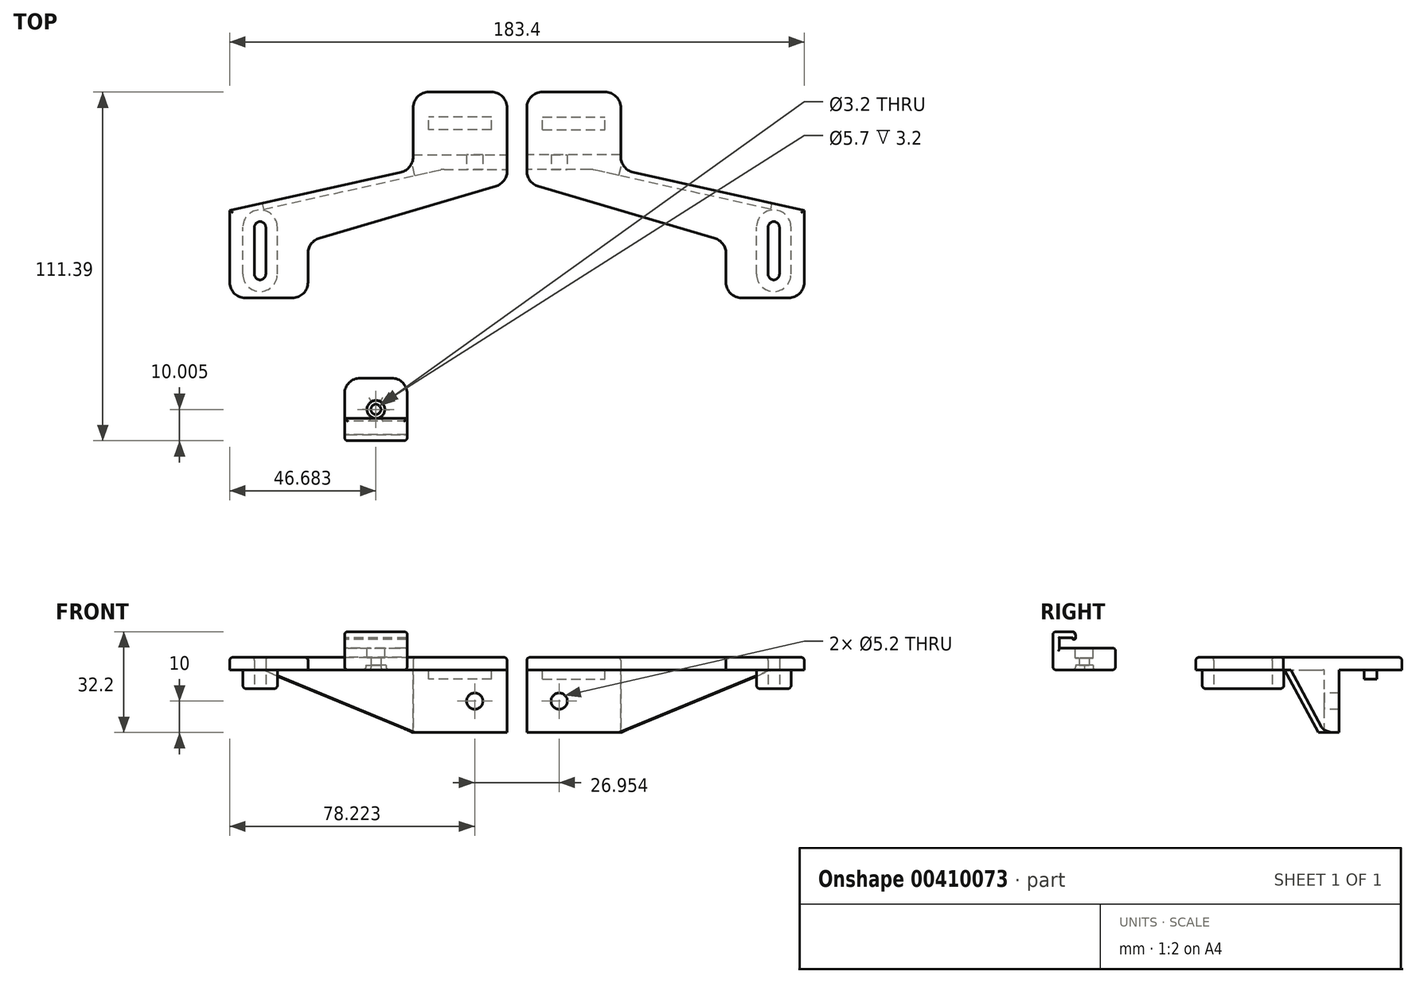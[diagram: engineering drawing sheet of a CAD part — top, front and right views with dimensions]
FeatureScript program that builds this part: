
annotation { "Feature Type Name" : "Feature", "Feature Type Description" : "" }
export const myFeature = defineFeature(function(context is Context, id is Id, definition is map)
    precondition{}
    {
        {
            var Q0;
            Q0=qCreatedBy(makeId("Top.planeOp"),FACE);
            var sketch = newSketch(context, id + "F0", { "sketchPlane" : qUnion([Q0])});
            skLineSegment(sketch, "E0", {"start": v(-33.14, 37.77) * mm, "end": v(-3.14, 37.77) * mm});
            skLineSegment(sketch, "E1", {"start": v(-3.14, 37.77) * mm, "end": v(-3.14, 8.77) * mm});
            skLineSegment(sketch, "E2", {"start": v(-33.14, 13.06) * mm, "end": v(-33.14, 37.77) * mm});
            skCircle(sketch, "E3", {"center": v(-81.98, -20.43) * mm, "radius": 1.8 * mm});
            skCircle(sketch, "E4", {"center": v(-81.98, -5.43) * mm, "radius": 1.8 * mm});
            skLineSegment(sketch, "E5", {"start": v(-83.78, -5.43) * mm, "end": v(-83.78, -20.43) * mm});
            skLineSegment(sketch, "E6", {"start": v(-80.18, -5.43) * mm, "end": v(-80.18, -20.43) * mm});
            skLineSegment(sketch, "E7", {"start": v(-33.14, 13.06) * mm, "end": v(-91.7, 0) * mm});
            skLineSegment(sketch, "E8", {"start": v(-91.7, 0) * mm, "end": v(-91.7, -28) * mm});
            skLineSegment(sketch, "E9", {"start": v(-91.7, -28) * mm, "end": v(-66.7, -28) * mm});
            skLineSegment(sketch, "E10", {"start": v(-66.7, -28) * mm, "end": v(-66.7, -10) * mm});
            skPoint(sketch, "E11.orphan", {"position": v(-33.14, -51.89) * mm});
            skLineSegment(sketch, "E12", {"start": v(-66.7, -10) * mm, "end": v(-3.14, 8.77) * mm});
            skSolve(sketch);
        }
        {
            var Q0;
            Q0=makeQuery(id+"F0.imprint","IMPRINT",FACE,{"disambiguationData":[TD([[makeQuery(id+"F0.imprint","IMPRINT",EDGE,{"derivedFrom":sQuery(id+"F0.wireOp",EDGE,"E0")}),-1.0]])]});
            extrude(context, id + "F1", {"entities" : qUnion([Q0]), "depth" : 4 * mm});
        }
        {
            var Q0;
            Q0=makeQuery(id+"F1.opExtrude","CAP_FACE",FACE,{"disambiguationData":[OSD([sQuery(id+"F0.wireOp",EDGE,"E0"),sQuery(id+"F0.wireOp",EDGE,"E1"),sQuery(id+"F0.wireOp",EDGE,"OpiebKvo-A6Ue-c39r-XeL3-1QtEK74ZUoIi"),sQuery(id+"F0.wireOp",EDGE,"yR2El9kB-Gpyi-T81o-eOrN-Ah2drDqhiUxG"),sQuery(id+"F0.wireOp",EDGE,"FQWpoFjm-FwZp-qIYe-eM8u-l31kpRkj3eQY"),sQuery(id+"F0.wireOp",EDGE,"E2"),sQuery(id+"F0.wireOp",EDGE,"E3"),sQuery(id+"F0.wireOp",EDGE,"E4"),sQuery(id+"F0.wireOp",EDGE,"E5"),sQuery(id+"F0.wireOp",EDGE,"E6")])],"isStart":true});
            var sketch = newSketch(context, id + "F2", { "sketchPlane" : qUnion([Q0])});
            skLineSegment(sketch, "E13", {"start": v(-3.14, -37.77) * mm, "end": v(-33.14, -37.77) * mm});
            skLineSegment(sketch, "E14.bottom", {"start": v(-8.14, -25.77) * mm, "end": v(-28.14, -25.77) * mm});
            skLineSegment(sketch, "E14.top", {"start": v(-8.14, -29.77) * mm, "end": v(-28.14, -29.77) * mm});
            skLineSegment(sketch, "E14.left", {"start": v(-8.14, -25.77) * mm, "end": v(-8.14, -29.77) * mm});
            skLineSegment(sketch, "E14.right", {"start": v(-28.14, -25.77) * mm, "end": v(-28.14, -29.77) * mm});
            skCircle(sketch, "E15", {"center": v(-81.98, 20.43) * mm, "radius": 5.5 * mm});
            skCircle(sketch, "E16", {"center": v(-81.98, 5.43) * mm, "radius": 5.5 * mm});
            skLineSegment(sketch, "E17", {"start": v(-87.48, 20.43) * mm, "end": v(-87.48, 5.43) * mm});
            skLineSegment(sketch, "E18", {"start": v(-76.48, 20.43) * mm, "end": v(-76.48, 5.43) * mm});
            skLineSegment(sketch, "E19", {"start": v(-33.14, -17.77) * mm, "end": v(-3.14, -17.77) * mm});
            skLineSegment(sketch, "E20", {"start": v(-33.14, -13.06) * mm, "end": v(-3.14, -13.06) * mm});
            skLineSegment(sketch, "E21", {"start": v(-81.38, -0.22) * mm, "end": v(-23.81, -13.06) * mm});
            skLineSegment(sketch, "E22", {"start": v(-53.1, -6.53) * mm, "end": v(-49.7, 4.98) * mm});
            skPoint(sketch, "E23", {"position": v(-81.38, -0.22) * mm});
            skLineSegment(sketch, "E24", {"start": v(-81.38, -0.22) * mm, "end": v(-81.82, -2.2) * mm});
            skSolve(sketch);
        }
        {
            var Q0;
            {var subQ0=sQuery(id+"F2.wireOp",EDGE,"E19");Q0=makeQuery(id+"F2.imprint","IMPRINT",FACE,{"disambiguationData":[TD([[makeQuery(id+"F2.imprint","IMPRINT",EDGE,{"derivedFrom":subQ0}),1.0]])]});}
            var Q1;
            Q1=makeQuery(id+"F2.imprint","IMPRINT",FACE,{"disambiguationData":[TD([[makeQuery(id+"F2.imprint","IMPRINT",EDGE,{"derivedFrom":sQuery(id+"F2.wireOp",EDGE,"BE3oNBv8-QwqM-P6IJ-gh2R-psUP1UZXCGw2")}),-1.0]])]});
            var Q2;
            {var subQ1=makeQuery(id+"F1.opExtrude","CAP_EDGE",EDGE,{"disambiguationData":[OSD([sQuery(id+"F0.wireOp",EDGE,"E7")])],"isStart":true});Q2=makeQuery(id+"F2.imprint","IMPRINT",FACE,{"disambiguationData":[TD([[makeQuery(id+"F2.imprint","IMPRINT",EDGE,{"derivedFrom":subQ1}),-1.0]])]});}
            extrude(context, id + "F3", {"entities" : qUnion([Q0, Q1, Q2]), "operationType" : NewBodyOperationType.ADD, "offsetDistance" : 25 * mm, "depth" : 20 * mm});
        }
        {
            var Q0;
            Q0=makeQuery(id+"F2.imprint","IMPRINT",FACE,{"disambiguationData":[TD([[makeQuery(id+"F2.imprint","IMPRINT",EDGE,{"derivedFrom":sQuery(id+"F2.wireOp",EDGE,"E14.bottom")}),1.0]])]});
            extrude(context, id + "F4", {"entities" : qUnion([Q0]), "operationType" : NewBodyOperationType.ADD, "depth" : 3 * mm});
        }
        {
            var Q0;
            Q0=makeQuery(id+"F3.opExtrude","SWEPT_FACE",FACE,{"disambiguationData":[OSD([sQuery(id+"F2.wireOp",EDGE,"E20")])]});
            var sketch = newSketch(context, id + "F5", { "sketchPlane" : qUnion([Q0])});
            skCircle(sketch, "E25", {"center": v(-13.48, -10) * mm, "radius": 2.6 * mm});
            skPoint(sketch, "E25.centerSnap0", {"position": v(-3.14, -10) * mm});
            skPoint(sketch, "E25.centerSnap1", {"position": v(-13.48, 0) * mm});
            skSolve(sketch);
        }
        {
            var Q0;
            Q0=makeQuery(id+"F5.imprint","IMPRINT",FACE,{"disambiguationData":[TD([[makeQuery(id+"F5.imprint","IMPRINT",EDGE,{"derivedFrom":sQuery(id+"F5.wireOp",EDGE,"UfRkS8na-2ZS5-7JHC-9wZ1-n38dNGz8aJN5")}),1.0]])]});
            var Q1;
            Q1=makeQuery(id+"F5.imprint","IMPRINT",FACE,{"disambiguationData":[TD([[makeQuery(id+"F5.imprint","IMPRINT",EDGE,{"derivedFrom":sQuery(id+"F5.wireOp",EDGE,"E25")}),1.0]])]});
            extrude(context, id + "F6", {"entities" : qUnion([Q0, Q1]), "operationType" : NewBodyOperationType.REMOVE, "endBound" : BoundingType.THROUGH_ALL, "oppositeDirection" : true, "depth" : 25 * mm});
        }
        {
            var Q0;
            {var subQ0=makeQuery(id+"F1.opExtrude","CAP_EDGE",EDGE,{"disambiguationData":[OSD([sQuery(id+"F0.wireOp",EDGE,"E3")])],"isStart":true});Q0=makeQuery(id+"F2.imprint","IMPRINT",FACE,{"disambiguationData":[TD([[makeQuery(id+"F2.imprint","IMPRINT",EDGE,{"derivedFrom":subQ0}),1.0]])]});}
            var Q1;
            {var subQ0=sQuery(id+"F2.wireOp",EDGE,"E17");Q1=makeQuery(id+"F2.imprint","IMPRINT",FACE,{"disambiguationData":[TD([[makeQuery(id+"F2.imprint","IMPRINT",EDGE,{"derivedFrom":subQ0}),1.0]])]});}
            var Q2;
            {var subQ0=makeQuery(id+"F1.opExtrude","CAP_EDGE",EDGE,{"disambiguationData":[OSD([sQuery(id+"F0.wireOp",EDGE,"E4")])],"isStart":true});Q2=makeQuery(id+"F2.imprint","IMPRINT",FACE,{"disambiguationData":[TD([[makeQuery(id+"F2.imprint","IMPRINT",EDGE,{"derivedFrom":subQ0}),1.0]])]});}
            var Q3;
            {var subQ0=sQuery(id+"F2.wireOp",EDGE,"E18");Q3=makeQuery(id+"F2.imprint","IMPRINT",FACE,{"disambiguationData":[TD([[makeQuery(id+"F2.imprint","IMPRINT",EDGE,{"derivedFrom":subQ0}),-1.0]])]});}
            extrude(context, id + "F7", {"entities" : qUnion([Q0, Q1, Q2, Q3]), "operationType" : NewBodyOperationType.ADD, "depth" : 6 * mm});
        }
        {
            var Q0;
            Q0=makeQuery(id+"F1.opExtrude","SWEPT_EDGE",EDGE,{"disambiguationData":[OSD([sQuery(id+"F0.wireOp",EDGE,"E0"),sQuery(id+"F0.wireOp",EDGE,"E1")])]});
            var Q1;
            Q1=makeQuery(id+"F1.opExtrude","SWEPT_EDGE",EDGE,{"disambiguationData":[OSD([sQuery(id+"F0.wireOp",EDGE,"E0"),sQuery(id+"F0.wireOp",EDGE,"E2")])]});
            var Q2;
            Q2=makeQuery(id+"F1.opExtrude","SWEPT_EDGE",EDGE,{"disambiguationData":[OSD([sQuery(id+"F0.wireOp",EDGE,"FQWpoFjm-FwZp-qIYe-eM8u-l31kpRkj3eQY"),sQuery(id+"F0.wireOp",EDGE,"E2")])]});
            var Q3;
            Q3=makeQuery(id+"F1.opExtrude","SWEPT_EDGE",EDGE,{"disambiguationData":[OSD([sQuery(id+"F0.wireOp",EDGE,"yR2El9kB-Gpyi-T81o-eOrN-Ah2drDqhiUxG"),sQuery(id+"F0.wireOp",EDGE,"FQWpoFjm-FwZp-qIYe-eM8u-l31kpRkj3eQY")])]});
            var Q4;
            Q4=makeQuery(id+"F1.opExtrude","SWEPT_EDGE",EDGE,{"disambiguationData":[OSD([sQuery(id+"F0.wireOp",EDGE,"OpiebKvo-A6Ue-c39r-XeL3-1QtEK74ZUoIi"),sQuery(id+"F0.wireOp",EDGE,"yR2El9kB-Gpyi-T81o-eOrN-Ah2drDqhiUxG")])]});
            var Q5;
            Q5=makeQuery(id+"F1.opExtrude","SWEPT_EDGE",EDGE,{"disambiguationData":[OSD([sQuery(id+"F0.wireOp",EDGE,"E1"),sQuery(id+"F0.wireOp",EDGE,"OpiebKvo-A6Ue-c39r-XeL3-1QtEK74ZUoIi")])]});
            var Q6;
            Q6=makeQuery(id+"F3.opExtrude","SWEPT_EDGE",EDGE,{"disambiguationData":[OSD([sQuery(id+"F2.wireOp",EDGE,"E20"),sQuery(id+"F2.wireOp",EDGE,"E21")])]});
            var Q7;
            Q7=makeQuery(id+"F1.opExtrude","SWEPT_EDGE",EDGE,{"disambiguationData":[OSD([sQuery(id+"F0.wireOp",EDGE,"E10"),sQuery(id+"F0.wireOp",EDGE,"E12")])]});
            var Q8;
            Q8=makeQuery(id+"F1.opExtrude","SWEPT_EDGE",EDGE,{"disambiguationData":[OSD([sQuery(id+"F0.wireOp",EDGE,"E9"),sQuery(id+"F0.wireOp",EDGE,"E10")])]});
            var Q9;
            Q9=makeQuery(id+"F1.opExtrude","SWEPT_EDGE",EDGE,{"disambiguationData":[OSD([sQuery(id+"F0.wireOp",EDGE,"E8"),sQuery(id+"F0.wireOp",EDGE,"E9")])]});
            fillet(context, id + "F8", {"entities" : qUnion([Q0, Q1, Q2, Q3, Q4, Q5, Q6, Q7, Q8, Q9]), "radius" : 5 * mm, "tangentPropagation" : true, "allowEdgeOverflow" : false});
        }
        {
            var Q0;
            Q0=makeQuery(id+"F1.opExtrude","CAP_FACE",FACE,{"disambiguationData":[OSD([sQuery(id+"F0.wireOp",EDGE,"E0"),sQuery(id+"F0.wireOp",EDGE,"E1"),sQuery(id+"F0.wireOp",EDGE,"OpiebKvo-A6Ue-c39r-XeL3-1QtEK74ZUoIi"),sQuery(id+"F0.wireOp",EDGE,"yR2El9kB-Gpyi-T81o-eOrN-Ah2drDqhiUxG"),sQuery(id+"F0.wireOp",EDGE,"FQWpoFjm-FwZp-qIYe-eM8u-l31kpRkj3eQY"),sQuery(id+"F0.wireOp",EDGE,"E2"),sQuery(id+"F0.wireOp",EDGE,"E3"),sQuery(id+"F0.wireOp",EDGE,"E4"),sQuery(id+"F0.wireOp",EDGE,"E5"),sQuery(id+"F0.wireOp",EDGE,"E6")])],"isStart":false});
            var Q1;
            Q1=makeQuery(id+"F3.opExtrude","CAP_EDGE",EDGE,{"disambiguationData":[OSD([sQuery(id+"F2.wireOp",EDGE,"E13")])],"isStart":true});
            var Q2;
            Q2=makeQuery(id+"F7.opExtrude","CAP_EDGE",EDGE,{"disambiguationData":[OSD([sQuery(id+"F2.wireOp",EDGE,"E17")])],"isStart":true});
            var Q3;
            Q3=makeQuery(id+"F7.opExtrude","CAP_EDGE",EDGE,{"disambiguationData":[OSD([sQuery(id+"F2.wireOp",EDGE,"E17")])],"isStart":false});
            fillet(context, id + "F9", {"entities" : qUnion([Q0, Q1, Q2, Q3]), "radius" : 1 * mm, "tangentPropagation" : true, "allowEdgeOverflow" : false});
        }
        {
            var Q0;
            Q0=makeQuery(id+"F3.opExtrude","CAP_EDGE",EDGE,{"disambiguationData":[OSD([sQuery(id+"F2.wireOp",EDGE,"E24")])],"isStart":false});
            chamfer(context, id + "F10", {"entities" : qUnion([Q0]), "chamferType" : ChamferType.OFFSET_ANGLE, "width" : 50 * mm, "oppositeDirection" : false, "angle" : 22 * degree, "tangentPropagation" : true});
        }
        {
            var Q0;
            Q0=makeQuery(id+"F1.opExtrude","SWEPT_BODY",BODY,{"disambiguationData":[OSD([sQuery(id+"F0.wireOp",EDGE,"E0"),sQuery(id+"F0.wireOp",EDGE,"E1"),sQuery(id+"F0.wireOp",EDGE,"OpiebKvo-A6Ue-c39r-XeL3-1QtEK74ZUoIi"),sQuery(id+"F0.wireOp",EDGE,"yR2El9kB-Gpyi-T81o-eOrN-Ah2drDqhiUxG"),sQuery(id+"F0.wireOp",EDGE,"FQWpoFjm-FwZp-qIYe-eM8u-l31kpRkj3eQY"),sQuery(id+"F0.wireOp",EDGE,"E2"),sQuery(id+"F0.wireOp",EDGE,"E3"),sQuery(id+"F0.wireOp",EDGE,"E4"),sQuery(id+"F0.wireOp",EDGE,"E5"),sQuery(id+"F0.wireOp",EDGE,"E6")])]});
            var Q1;
            Q1=qCreatedBy(makeId("Right.planeOp"),FACE);
            mirror(context, id + "F11", {"entities" : qUnion([Q0]), "mirrorPlane" : qUnion([Q1])});
        }
        {
            var Q0;
            Q0=qCreatedBy(makeId("Top.planeOp"),FACE);
            var sketch = newSketch(context, id + "F12", { "sketchPlane" : qUnion([Q0])});
            skLineSegment(sketch, "E26.bottom", {"start": v(-55.02, -53.62) * mm, "end": v(-35.02, -53.62) * mm});
            skLineSegment(sketch, "E26.top", {"start": v(-55.02, -73.62) * mm, "end": v(-35.02, -73.62) * mm});
            skLineSegment(sketch, "E26.left", {"start": v(-55.02, -53.62) * mm, "end": v(-55.02, -73.62) * mm});
            skLineSegment(sketch, "E26.right", {"start": v(-35.02, -53.62) * mm, "end": v(-35.02, -73.62) * mm});
            skCircle(sketch, "E27", {"center": v(-45.02, -63.62) * mm, "radius": 1.6 * mm});
            skPoint(sketch, "E27.centerSnap0", {"position": v(-55.02, -63.62) * mm});
            skPoint(sketch, "E27.centerSnap1", {"position": v(-45.02, -53.62) * mm});
            skSolve(sketch);
        }
        {
            var Q0;
            Q0=qSketchRegion(id+"F12",true);
            extrude(context, id + "F13", {"entities" : qUnion([Q0]), "depth" : 7 * mm});
        }
        {
            var Q0;
            Q0=makeQuery(id+"F13.opExtrude","CAP_FACE",FACE,{"disambiguationData":[OSD([sQuery(id+"F12.wireOp",EDGE,"E26.bottom"),sQuery(id+"F12.wireOp",EDGE,"E26.top"),sQuery(id+"F12.wireOp",EDGE,"E26.left"),sQuery(id+"F12.wireOp",EDGE,"E26.right"),sQuery(id+"F12.wireOp",EDGE,"E27")])],"isStart":false});
            var sketch = newSketch(context, id + "F14", { "sketchPlane" : qUnion([Q0])});
            skCircle(sketch, "E28", {"center": v(-45.02, -63.62) * mm, "radius": 2.85 * mm});
            skLineSegment(sketch, "E29", {"start": v(-55.02, -71.62) * mm, "end": v(-35.02, -71.62) * mm});
            skSolve(sketch);
        }
        {
            var Q0;
            Q0=makeQuery(id+"F14.imprint","IMPRINT",FACE,{"disambiguationData":[TD([[makeQuery(id+"F14.imprint","IMPRINT",EDGE,{"derivedFrom":sQuery(id+"F14.wireOp",EDGE,"E28")}),1.0]])]});
            extrude(context, id + "F15", {"entities" : qUnion([Q0]), "operationType" : NewBodyOperationType.REMOVE, "oppositeDirection" : true, "depth" : 3.2 * mm});
        }
        {
            var Q0;
            Q0=makeQuery(id+"F13.opExtrude","CAP_FACE",FACE,{"disambiguationData":[OSD([sQuery(id+"F12.wireOp",EDGE,"E26.bottom"),sQuery(id+"F12.wireOp",EDGE,"E26.top"),sQuery(id+"F12.wireOp",EDGE,"E26.left"),sQuery(id+"F12.wireOp",EDGE,"E26.right"),sQuery(id+"F12.wireOp",EDGE,"E27")])],"isStart":true});
            var sketch = newSketch(context, id + "F16", { "sketchPlane" : qUnion([Q0])});
            skCircle(sketch, "E30.cCircle", {"center": v(-45.02, 63.62) * mm, "radius": 2.8 * mm, "construction": true});
            skLineSegment(sketch, "E30.0", {"start": v(-46.63, 66.42) * mm, "end": v(-43.4, 66.42) * mm});
            skLineSegment(sketch, "E30.1", {"start": v(-43.4, 66.42) * mm, "end": v(-41.78, 63.62) * mm});
            skLineSegment(sketch, "E30.2", {"start": v(-41.78, 63.62) * mm, "end": v(-43.4, 60.82) * mm});
            skLineSegment(sketch, "E30.3", {"start": v(-43.4, 60.82) * mm, "end": v(-46.63, 60.82) * mm});
            skLineSegment(sketch, "E30.4", {"start": v(-46.63, 60.82) * mm, "end": v(-48.25, 63.62) * mm});
            skLineSegment(sketch, "E30.5", {"start": v(-48.25, 63.62) * mm, "end": v(-46.63, 66.42) * mm});
            skPoint(sketch, "E30.0.midPoint", {"position": v(-45.02, 66.42) * mm});
            skSolve(sketch);
        }
        {
            var Q0;
            Q0=makeQuery(id+"F16.imprint","IMPRINT",FACE,{"disambiguationData":[TD([[makeQuery(id+"F16.imprint","IMPRINT",EDGE,{"derivedFrom":sQuery(id+"F16.wireOp",EDGE,"E30.0")}),-1.0]])]});
            extrude(context, id + "F17", {"entities" : qUnion([Q0]), "operationType" : NewBodyOperationType.REMOVE, "oppositeDirection" : true, "depth" : 1.5 * mm});
        }
        {
            var Q0;
            {var subQ0=sQuery(id+"F14.wireOp",EDGE,"E29");Q0=makeQuery(id+"F14.imprint","IMPRINT",FACE,{"disambiguationData":[TD([[makeQuery(id+"F14.imprint","IMPRINT",EDGE,{"derivedFrom":subQ0}),-1.0]])]});}
            extrude(context, id + "F18", {"entities" : qUnion([Q0]), "operationType" : NewBodyOperationType.ADD, "depth" : 5.2 * mm});
        }
        {
            var Q0;
            Q0=makeQuery(id+"F18.opExtrude","SWEPT_FACE",FACE,{"disambiguationData":[OSD([sQuery(id+"F14.wireOp",EDGE,"E29")])]});
            var sketch = newSketch(context, id + "F19", { "sketchPlane" : qUnion([Q0])});
            skLineSegment(sketch, "E31", {"start": v(35.02, 10.2) * mm, "end": v(55.02, 10.2) * mm});
            skSolve(sketch);
        }
        {
            var Q0;
            {var subQ0=sQuery(id+"F19.wireOp",EDGE,"E31");Q0=makeQuery(id+"F19.imprint","IMPRINT",FACE,{"disambiguationData":[TD([[makeQuery(id+"F19.imprint","IMPRINT",EDGE,{"derivedFrom":subQ0}),1.0]])]});}
            extrude(context, id + "F20", {"entities" : qUnion([Q0]), "operationType" : NewBodyOperationType.ADD, "depth" : 5.2 * mm});
        }
        {
            var Q0;
            Q0=makeQuery(id+"F20.opExtrude","SWEPT_FACE",FACE,{"disambiguationData":[OSD([sQuery(id+"F19.wireOp",EDGE,"E31")])]});
            var sketch = newSketch(context, id + "F21", { "sketchPlane" : qUnion([Q0])});
            skLineSegment(sketch, "E32", {"start": v(-35.02, 67.42) * mm, "end": v(-55.02, 67.42) * mm});
            skPoint(sketch, "E32.endSnap0", {"position": v(-55.02, 69.02) * mm});
            skSolve(sketch);
        }
        {
            var Q0;
            {var subQ0=sQuery(id+"F21.wireOp",EDGE,"E32");Q0=makeQuery(id+"F21.imprint","IMPRINT",FACE,{"disambiguationData":[TD([[makeQuery(id+"F21.imprint","IMPRINT",EDGE,{"derivedFrom":subQ0}),1.0]])]});}
            extrude(context, id + "F22", {"entities" : qUnion([Q0]), "operationType" : NewBodyOperationType.ADD, "depth" : 0.4 * mm});
        }
        {
            var Q0;
            Q0=makeQuery(id+"F13.opExtrude","SWEPT_EDGE",EDGE,{"disambiguationData":[OSD([sQuery(id+"F12.wireOp",EDGE,"E26.bottom"),sQuery(id+"F12.wireOp",EDGE,"E26.right")])]});
            var Q1;
            Q1=makeQuery(id+"F13.opExtrude","SWEPT_EDGE",EDGE,{"disambiguationData":[OSD([sQuery(id+"F12.wireOp",EDGE,"E26.bottom"),sQuery(id+"F12.wireOp",EDGE,"E26.left")])]});
            fillet(context, id + "F23", {"entities" : qUnion([Q0, Q1]), "radius" : 5 * mm, "tangentPropagation" : true, "allowEdgeOverflow" : false});
        }
        {
            var Q0;
            Q0=makeQuery(id+"F15.boolean.opBoolean","COPY",EDGE,{"derivedFrom":makeQuery(id+"F15.opExtrude","CAP_EDGE",EDGE,{"disambiguationData":[OSD([sQuery(id+"F14.wireOp",EDGE,"E28")])],"isStart":true})});
            var Q1;
            Q1=makeQuery(id+"F18.opExtrude","CAP_EDGE",EDGE,{"disambiguationData":[OSD([sQuery(id+"F12.wireOp",EDGE,"E26.top")])],"isStart":false});
            var Q2;
            Q2=makeQuery(id+"F20.opExtrude","CAP_EDGE",EDGE,{"disambiguationData":[OSD([sQuery(id+"F14.wireOp",EDGE,"E29")])],"isStart":false});
            var Q3;
            Q3=makeQuery(id+"F13.opExtrude","CAP_EDGE",EDGE,{"disambiguationData":[OSD([sQuery(id+"F12.wireOp",EDGE,"E26.right")])],"isStart":false});
            var Q4;
            Q4=makeQuery(id+"F13.opExtrude","CAP_EDGE",EDGE,{"disambiguationData":[OSD([sQuery(id+"F12.wireOp",EDGE,"E26.bottom")])],"isStart":false});
            var Q5;
            {var subQ0=sQuery(id+"F12.wireOp",EDGE,"E26.right");var subQ1=sQuery(id+"F12.wireOp",EDGE,"E26.bottom");Q5=makeQuery(id+"F23.opFillet","BLEND_EDGE",EDGE,{"blendedFrom":[makeQuery(id+"F13.opExtrude","SWEPT_EDGE",EDGE,{"disambiguationData":[OSD([subQ1,subQ0])]}),makeQuery(id+"F13.opExtrude","CAP_FACE",FACE,{"disambiguationData":[OSD([subQ1,sQuery(id+"F12.wireOp",EDGE,"E26.top"),sQuery(id+"F12.wireOp",EDGE,"E26.left"),subQ0,sQuery(id+"F12.wireOp",EDGE,"E27")])],"isStart":false})],"blendedInto":[makeQuery(id+"F13.opExtrude","CAP_FACE",FACE,{"disambiguationData":[OSD([subQ1,sQuery(id+"F12.wireOp",EDGE,"E26.top"),sQuery(id+"F12.wireOp",EDGE,"E26.left"),subQ0,sQuery(id+"F12.wireOp",EDGE,"E27")])],"isStart":false})]});}
            var Q6;
            Q6=makeQuery(id+"F13.opExtrude","CAP_EDGE",EDGE,{"disambiguationData":[OSD([sQuery(id+"F12.wireOp",EDGE,"E26.left")])],"isStart":false});
            var Q7;
            {var subQ0=sQuery(id+"F12.wireOp",EDGE,"E26.left");var subQ1=sQuery(id+"F12.wireOp",EDGE,"E26.bottom");Q7=makeQuery(id+"F23.opFillet","BLEND_EDGE",EDGE,{"blendedFrom":[makeQuery(id+"F13.opExtrude","SWEPT_EDGE",EDGE,{"disambiguationData":[OSD([subQ1,subQ0])]}),makeQuery(id+"F13.opExtrude","CAP_FACE",FACE,{"disambiguationData":[OSD([subQ1,sQuery(id+"F12.wireOp",EDGE,"E26.top"),subQ0,sQuery(id+"F12.wireOp",EDGE,"E26.right"),sQuery(id+"F12.wireOp",EDGE,"E27")])],"isStart":false})],"blendedInto":[makeQuery(id+"F13.opExtrude","CAP_FACE",FACE,{"disambiguationData":[OSD([subQ1,sQuery(id+"F12.wireOp",EDGE,"E26.top"),subQ0,sQuery(id+"F12.wireOp",EDGE,"E26.right"),sQuery(id+"F12.wireOp",EDGE,"E27")])],"isStart":false})]});}
            var Q8;
            Q8=makeQuery(id+"F13.opExtrude","CAP_FACE",FACE,{"disambiguationData":[OSD([sQuery(id+"F12.wireOp",EDGE,"E26.bottom"),sQuery(id+"F12.wireOp",EDGE,"E26.top"),sQuery(id+"F12.wireOp",EDGE,"E26.left"),sQuery(id+"F12.wireOp",EDGE,"E26.right"),sQuery(id+"F12.wireOp",EDGE,"E27")])],"isStart":true});
            var Q9;
            {var subQ0=sQuery(id+"F12.wireOp",EDGE,"E26.right");var subQ1=sQuery(id+"F12.wireOp",EDGE,"E26.top");Q9=makeQuery(id+"F18.boolean.opBoolean","MERGE",EDGE,{"derivedFrom":[makeQuery(id+"F13.opExtrude","SWEPT_EDGE",EDGE,{"disambiguationData":[OSD([subQ1,subQ0])]}),makeQuery(id+"F18.opExtrude","SWEPT_EDGE",EDGE,{"disambiguationData":[OSD([subQ1,subQ0])]})]});}
            var Q10;
            {var subQ0=sQuery(id+"F12.wireOp",EDGE,"E26.left");var subQ1=sQuery(id+"F12.wireOp",EDGE,"E26.top");Q10=makeQuery(id+"F18.boolean.opBoolean","MERGE",EDGE,{"derivedFrom":[makeQuery(id+"F13.opExtrude","SWEPT_EDGE",EDGE,{"disambiguationData":[OSD([subQ1,subQ0])]}),makeQuery(id+"F18.opExtrude","SWEPT_EDGE",EDGE,{"disambiguationData":[OSD([subQ1,subQ0])]})]});}
            var Q11;
            {var subQ0=sQuery(id+"F12.wireOp",EDGE,"E26.left");Q11=makeQuery(id+"F20.boolean.opBoolean","MERGE",EDGE,{"derivedFrom":[makeQuery(id+"F18.opExtrude","CAP_EDGE",EDGE,{"disambiguationData":[OSD([subQ0])],"isStart":false}),makeQuery(id+"F20.opExtrude","SWEPT_EDGE",EDGE,{"disambiguationData":[OSD([subQ0,sQuery(id+"F14.wireOp",EDGE,"E29")])]})]});}
            var Q12;
            {var subQ0=sQuery(id+"F12.wireOp",EDGE,"E26.right");Q12=makeQuery(id+"F20.boolean.opBoolean","MERGE",EDGE,{"derivedFrom":[makeQuery(id+"F18.opExtrude","CAP_EDGE",EDGE,{"disambiguationData":[OSD([subQ0])],"isStart":false}),makeQuery(id+"F20.opExtrude","SWEPT_EDGE",EDGE,{"disambiguationData":[OSD([subQ0,sQuery(id+"F14.wireOp",EDGE,"E29")])]})]});}
            fillet(context, id + "F24", {"entities" : qUnion([Q0, Q1, Q2, Q3, Q4, Q5, Q6, Q7, Q8, Q9, Q10, Q11, Q12]), "radius" : 1 * mm, "allowEdgeOverflow" : false});
        }
        {
            var Q0;
            Q0=makeQuery(id+"F18.opExtrude","SWEPT_EDGE",EDGE,{"disambiguationData":[OSD([sQuery(id+"F12.wireOp",EDGE,"E26.right"),sQuery(id+"F14.wireOp",EDGE,"E29")])]});
            var Q1;
            Q1=makeQuery(id+"F20.opExtrude","SWEPT_EDGE",EDGE,{"disambiguationData":[OSD([sQuery(id+"F12.wireOp",EDGE,"E26.right"),sQuery(id+"F14.wireOp",EDGE,"E29"),sQuery(id+"F19.wireOp",EDGE,"E31")])]});
            var Q2;
            Q2=makeQuery(id+"F22.opExtrude","CAP_EDGE",EDGE,{"disambiguationData":[OSD([sQuery(id+"F12.wireOp",EDGE,"E26.right"),sQuery(id+"F14.wireOp",EDGE,"E29"),sQuery(id+"F19.wireOp",EDGE,"E31")])],"isStart":false});
            var Q3;
            Q3=makeQuery(id+"F22.opExtrude","SWEPT_EDGE",EDGE,{"disambiguationData":[OSD([sQuery(id+"F12.wireOp",EDGE,"E26.right"),sQuery(id+"F14.wireOp",EDGE,"E29"),sQuery(id+"F19.wireOp",EDGE,"E31"),sQuery(id+"F21.wireOp",EDGE,"E32")])]});
            var Q4;
            {var subQ0=sQuery(id+"F14.wireOp",EDGE,"E29");var subQ1=sQuery(id+"F12.wireOp",EDGE,"E26.right");Q4=makeQuery(id+"F22.boolean.opBoolean","MERGE",EDGE,{"derivedFrom":[makeQuery(id+"F20.opExtrude","CAP_EDGE",EDGE,{"disambiguationData":[OSD([subQ1,subQ0])],"isStart":false}),makeQuery(id+"F22.opExtrude","SWEPT_EDGE",EDGE,{"disambiguationData":[OSD([subQ1,subQ0,sQuery(id+"F19.wireOp",EDGE,"E31")])]})]});}
            var Q5;
            Q5=makeQuery(id+"F22.opExtrude","CAP_EDGE",EDGE,{"disambiguationData":[OSD([sQuery(id+"F21.wireOp",EDGE,"E32")])],"isStart":false});
            var Q6;
            Q6=makeQuery(id+"F22.opExtrude","CAP_EDGE",EDGE,{"disambiguationData":[OSD([sQuery(id+"F19.wireOp",EDGE,"E31")])],"isStart":false});
            var Q7;
            {var subQ0=sQuery(id+"F14.wireOp",EDGE,"E29");var subQ1=sQuery(id+"F12.wireOp",EDGE,"E26.left");Q7=makeQuery(id+"F22.boolean.opBoolean","MERGE",EDGE,{"derivedFrom":[makeQuery(id+"F20.opExtrude","CAP_EDGE",EDGE,{"disambiguationData":[OSD([subQ1,subQ0])],"isStart":false}),makeQuery(id+"F22.opExtrude","SWEPT_EDGE",EDGE,{"disambiguationData":[OSD([subQ1,subQ0,sQuery(id+"F19.wireOp",EDGE,"E31")])]})]});}
            var Q8;
            Q8=makeQuery(id+"F22.opExtrude","CAP_EDGE",EDGE,{"disambiguationData":[OSD([sQuery(id+"F12.wireOp",EDGE,"E26.left"),sQuery(id+"F14.wireOp",EDGE,"E29"),sQuery(id+"F19.wireOp",EDGE,"E31")])],"isStart":false});
            var Q9;
            Q9=makeQuery(id+"F22.opExtrude","SWEPT_EDGE",EDGE,{"disambiguationData":[OSD([sQuery(id+"F12.wireOp",EDGE,"E26.left"),sQuery(id+"F14.wireOp",EDGE,"E29"),sQuery(id+"F19.wireOp",EDGE,"E31"),sQuery(id+"F21.wireOp",EDGE,"E32")])]});
            var Q10;
            Q10=makeQuery(id+"F20.opExtrude","SWEPT_EDGE",EDGE,{"disambiguationData":[OSD([sQuery(id+"F12.wireOp",EDGE,"E26.left"),sQuery(id+"F14.wireOp",EDGE,"E29"),sQuery(id+"F19.wireOp",EDGE,"E31")])]});
            fillet(context, id + "F25", {"entities" : qUnion([Q0, Q1, Q2, Q3, Q4, Q5, Q6, Q7, Q8, Q9, Q10]), "radius" : 0.2 * mm, "tangentPropagation" : true, "allowEdgeOverflow" : false});
        }
    });
